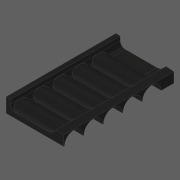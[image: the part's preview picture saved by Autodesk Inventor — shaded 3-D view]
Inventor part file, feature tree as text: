
AUTODESK INVENTOR PART (.ipt)
format: ipt  version: 2020 (Build 240168000, 168)  size: 2,801,152 bytes
history: native  units: in
note: dims shown in document units (in); Inventor stores cm internally (conversion verified against a paired STEP export)
features: other x35, extrude x21, loft x3, pattern_linear x3, fillet x2, plane x1, split x1, sketch x1, projected_geometry x1
ambient origin geometry x8: Origin, YZ Plane, XZ Plane, XY Plane, X Axis, Y Axis, Z Axis, Center Point
bodies: Body1 (feature_tree)
feature tree (68):
  other  "CrossSection1"
  other  "CrossSection2"
  other  "CrossSection3"
  other  "Whole"
  other  "Vertical Midplane"
  other  "Horizontal Midplane"
  extrude  "Block"  Depth=1.8125in
  extrude  "Hinge Protrusion"  Depth=1.8125in
  other  "Resonator Profile"
  extrude  "Resonator"  Depth=1.8125in
  extrude  "Resonator Cut"  TaperAngle=0.0deg  [1 undecoded]
  extrude  "Duct Cavity"  Depth=1.8125in
  other  "Duct Cavity Plane"
  loft  "Duct Entrance Loft"
  other  "Whistle Path Midplane"
  other  "Slit Loft To"
  loft  "Slit Loft"
  extrude  "Slit"  TaperAngle=0.0deg  [1 undecoded]
  other  "Fitting"
  extrude  "Edge Cut"  Depth=0.1969in
  other  "Edge Plane"
  other  "Edge Sketch"
  loft  "Edge Loft"
  extrude  "Edge"  TaperAngle=90.0deg  [1 undecoded]
  other  "Edge Cut Plane"
  extrude  "Spring Steel Slot"  Depth=1.8125in
  fillet  "Duct Fillet"  [1 undecoded]
  pattern_linear  "Channel Repetition"  Spacing1=0.2441in  [1 undecoded]
  extrude  "Edge Length Cut"  Depth=1.8125in
  other  "Tube Length Curve"
  extrude  "Long Tubes Length Cut"  Depth=1.8125in
  extrude  "Short Tubes Length Cut"  Depth=1.8125in
  extrude  "Whistle Walls"  Depth=1.8125in
  fillet  "Whistle Wall Fillet"  Radius=0.4921in
  pattern_linear  "Whistle Wall Repetition"  Spacing1=0.0197in  [1 undecoded]
  extrude  "End Caps"  Depth=1.8125in
  extrude  "Extra Block (for short notes)"  Depth=1.8125in
  other  "End Cap Tidying Plane"
  other  "End Cap Tidying Sketch"
  extrude  "End Cap Tidying"  Depth=1.8125in
  extrude  "End Cap Tidying (reverse)"  TaperAngle=0.0deg  [1 undecoded]
  pattern_linear  "End Cap Tidying Repetition"  Spacing1=0.2441in  [1 undecoded]
  extrude  "End Cap Tidying (edges)"  Depth=1.8125in
  extrude  "End Cap Tidying (edges, reverse)"  Depth=1.8125in
  other  "End-of-block Plane"
  extrude  "Manifold Slots"  Depth=1.8125in
  extrude  "Extension for Top C Key"  TaperAngle=0.0deg  [1 undecoded]
  other  "Split Plane"
  other  "Split for Printing"
  plane  "Work Plane14"
  split  "Split2"
  other  "Block Profile"
  other  "Fitting Sketch"
  other  "Duct Cavity Profile"
  other  "Duct Entrance Loft From"
  other  "Hinge Protrusion Sketch"
  other  "Edge Cut Sketch"
  other  "Edges3"
  other  "Edge Length Curve"
  other  "Whistle Wall Sketch"
  other  "2D Equation Curve10"
  other  "2D Equation Curve11"
  other  "Duct Entrance Loft To"
  other  "Slit Loft From"
  other  "Manifold Slot Sketch"
  other  "Spring Steel Slot Sketch"
  sketch  "Sketch27"  dims[d6=0.0in d7=9.8425in d9=0.4724in d20=0.3153in d21=0.0in d58=0.4882in d59=0.0in d62=2.3498in d63=0.0in d70=0.1969in d71=0.1292in d80=90.0deg d105=0.2362in d106=0.0in d109=0.2441in d111=0.1528in d112=0.1245in d114=0.1528in d115=0.2441in d118=0.4921in d148=0.0197in d150=0.2559in d151=0.8819in d152=0.4882in d154=0.0in d162=0.2441in d163=0.2362in d165=0.2441in d166=0.2461in d167=0.0in d171=0.2362in d174=0.4882in d175=0.4567in d176=0.0in d177=90.0deg d178=0.0in d179=90.0deg d185=0.3788in d186=0.0in d189=0.1954in d190=28.3465in d191=38.2021in d198=0.0803in d199=0.0in d200=0.0197in d201=0.0787in d202=-0.125in d203=0.7874in d206=0.2559in d209=0.0in d211=9.8425in d213=0.4724in d214=0.2362in d216=0.4567in d217=0.4882in d223=1.5748in d229=0.4882in d230=0.0in d234=0.4724in d235=0.4882in d237=0.2441in d239=1.4483in d240=0.0in d241=9.8425in d243=0.4724in d246=0.0394in d247=0.7043in d248=0.0in d249=0.2441in d250=11.8189in d251=0.0079in d252=28.3465in d253=38.2021in d254=28.3465in d255=38.2021in d256=-0.1575in d257=0.2362in d258=0.2151in d259=0.2441in d261=0.0in d262=90.0deg d263=0.0in d264=90.0deg d265=11.8268in d266=6.7754in d269=0.9992in d270=0.0in d271=0.9992in d272=0.0in d276=0.4882in d277=0.4567in d278=0.4882in d279=0.1954in d280=3.2088in d283=0.2362in d284=0.2441in d285=0.4486in d286=0.5118in d287=0.0in d288=90.0deg d289=0.0in d290=90.0deg d292=0.4882in d293=0.0in d294=1.5748in d295=0.4803in d299=0.5906in d300=0.0in d319=0.1299in d320=0.0787in d321=0.0669in d325=0.1299in d326=0.0787in d327=0.0669in d331=0.1299in d332=0.0787in d333=0.0669in d334=0.1299in d335=0.0787in d336=0.0669in d343=1.8898in d344=1.8898in d345=0.9449in d346=1.4173in d347=0.1299in d348=0.0787in d349=0.0669in d350=0.1299in d351=0.0787in d352=0.0669in d359=1.8898in d375=0.9449in d376=0.1299in d377=0.0787in d378=0.0669in d382=1.8898in d388=0.0317in d389=0.2559in d392=0.2072in d393=0.0in d396=0.2899in d397=0.0197in d398=0.0787in d399=0.0in d400=0.7874in d403=0.0618in d405=0.0197in d406=0.0787in d407=0.0in d408=0.7874in d410=0.1102in d411=0.0in d413=0.1969in d416=0.1095in d417=0.1575in d419=0.4882in d432=0.1412in d434=0.1875in d440=0.2441in d441=0.0in d442=1.5748in d443=0.0157in d444=45.0deg d445=0.4882in d448=0.2441in d451=0.1181in d452=0.5906in d453=0.1969in d457=0.122in d461=0.286in d462=0.0in d463=1.8125in d464=-2.6563in d137=0.0197in d138=0.0344in d139=0.0197in d140=0.0344in d207=0.0344in d208=0.0197in d267=0.0197in d268=0.0344in d281=0.0197in d282=0.0344in d414=0.0344in d415=0.0197in d425=0.0197in d426=0.0344in d427=0.0197in d428=0.0344in]
  projected_geometry  "Projected Loop5"
note: 9 required parameter values undecoded (feature->parameter linkage not recoverable at this tier; creation-order binding heuristic only, values carry confidence <= 0.55)
